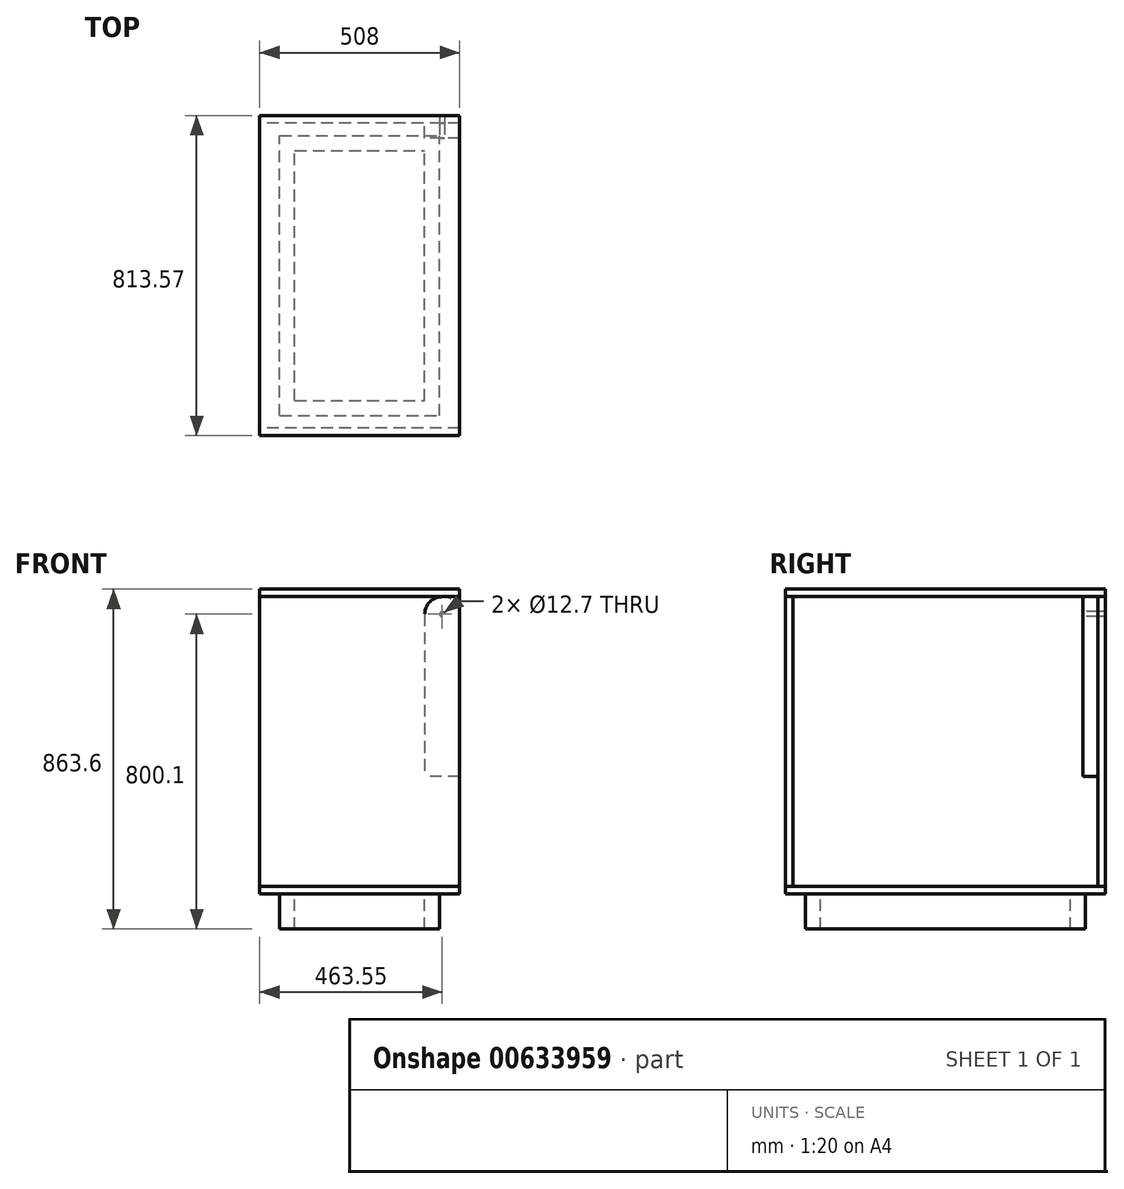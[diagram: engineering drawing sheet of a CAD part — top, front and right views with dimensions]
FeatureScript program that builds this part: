
annotation { "Feature Type Name" : "Feature", "Feature Type Description" : "" }
export const myFeature = defineFeature(function(context is Context, id is Id, definition is map)
    precondition{}
    {
        {
            var Q0;
            Q0=qCreatedBy(makeId("Front.planeOp"),FACE);
            var sketch = newSketch(context, id + "F0", { "sketchPlane" : qUnion([Q0])});
            skLineSegment(sketch, "E0.bottom", {"start": v(0, 0) * mm, "end": v(-508, 0) * mm});
            skLineSegment(sketch, "E0.top", {"start": v(0, -736.6) * mm, "end": v(-508, -736.6) * mm});
            skLineSegment(sketch, "E0.left", {"start": v(0, 0) * mm, "end": v(0, -736.6) * mm});
            skLineSegment(sketch, "E0.right", {"start": v(-508, 0) * mm, "end": v(-508, -736.6) * mm});
            skSolve(sketch);
        }
        {
            var Q0;
            Q0=makeQuery(id+"F0.imprint","IMPRINT",FACE,{"disambiguationData":[TD([[makeQuery(id+"F0.imprint","IMPRINT",EDGE,{"derivedFrom":sQuery(id+"F0.wireOp",EDGE,"E0.bottom")}),1.0]])]});
            extrude(context, id + "F1", {"entities" : qUnion([Q0]), "depth" : 19.05 * mm, "offsetDistance" : 25.4 * mm});
        }
        {
            var Q0;
            Q0=makeQuery(id+"F1.opExtrude","CAP_FACE",FACE,{"disambiguationData":[OSD([sQuery(id+"F0.wireOp",EDGE,"E0.bottom"),sQuery(id+"F0.wireOp",EDGE,"E0.top"),sQuery(id+"F0.wireOp",EDGE,"E0.left"),sQuery(id+"F0.wireOp",EDGE,"E0.right")])],"isStart":true});
            cPlane(context, id + "F2", {"entities" : qUnion([Q0]), "cplaneType" : CPlaneType.OFFSET, "offset" : 793.75 * mm, "width" : 152.4 * mm, "height" : 152.4 * mm});
        }
        {
            var Q0;
            Q0=qCreatedBy(makeId("Top.planeOp"),FACE);
            cPlane(context, id + "F3", {"entities" : qUnion([Q0]), "cplaneType" : CPlaneType.OFFSET, "offset" : 755.65 * mm, "oppositeDirection" : true, "width" : 152.4 * mm, "height" : 152.4 * mm});
        }
        {
            var Q0;
            Q0=qCreatedBy(id+"F2.planeOp",FACE);
            var sketch = newSketch(context, id + "F4", { "sketchPlane" : qUnion([Q0])});
            skLineSegment(sketch, "E1.bottom", {"start": v(0, 0) * mm, "end": v(508, 0) * mm});
            skLineSegment(sketch, "E1.top", {"start": v(0, -736.6) * mm, "end": v(508, -736.6) * mm});
            skLineSegment(sketch, "E1.left", {"start": v(0, 0) * mm, "end": v(0, -736.6) * mm});
            skLineSegment(sketch, "E1.right", {"start": v(508, 0) * mm, "end": v(508, -736.6) * mm});
            skSolve(sketch);
        }
        {
            var Q0;
            Q0=makeQuery(id+"F4.imprint","IMPRINT",FACE,{"disambiguationData":[TD([[makeQuery(id+"F4.imprint","IMPRINT",EDGE,{"derivedFrom":sQuery(id+"F4.wireOp",EDGE,"E1.bottom")}),-1.0]])]});
            extrude(context, id + "F5", {"entities" : qUnion([Q0]), "oppositeDirection" : true, "depth" : 19.05 * mm, "offsetDistance" : 25.4 * mm});
        }
        {
            var Q0;
            Q0=qCreatedBy(makeId("Top.planeOp"),FACE);
            var sketch = newSketch(context, id + "F6", { "sketchPlane" : qUnion([Q0])});
            skLineSegment(sketch, "E2.bottom", {"start": v(0, -18.96) * mm, "end": v(-508, -18.96) * mm});
            skLineSegment(sketch, "E2.top", {"start": v(0, 793.84) * mm, "end": v(-508, 793.84) * mm});
            skLineSegment(sketch, "E2.left", {"start": v(0, -18.96) * mm, "end": v(0, 793.84) * mm});
            skLineSegment(sketch, "E2.right", {"start": v(-508, -18.96) * mm, "end": v(-508, 793.84) * mm});
            skSolve(sketch);
        }
        {
            var Q0;
            Q0=makeQuery(id+"F6.imprint","IMPRINT",FACE,{"disambiguationData":[TD([[makeQuery(id+"F6.imprint","IMPRINT",EDGE,{"derivedFrom":sQuery(id+"F6.wireOp",EDGE,"E2.bottom")}),-1.0]])]});
            extrude(context, id + "F7", {"entities" : qUnion([Q0]), "depth" : 19.05 * mm, "offsetDistance" : 25.4 * mm});
        }
        {
            var Q0;
            Q0=qCreatedBy(id+"F3.planeOp",FACE);
            var sketch = newSketch(context, id + "F8", { "sketchPlane" : qUnion([Q0])});
            skLineSegment(sketch, "E3.bottom", {"start": v(0, -19.73) * mm, "end": v(-508, -19.73) * mm});
            skLineSegment(sketch, "E3.top", {"start": v(0, 793.07) * mm, "end": v(-508, 793.07) * mm});
            skLineSegment(sketch, "E3.left", {"start": v(0, -19.73) * mm, "end": v(0, 793.07) * mm});
            skLineSegment(sketch, "E3.right", {"start": v(-508, -19.73) * mm, "end": v(-508, 793.07) * mm});
            skSolve(sketch);
        }
        {
            var Q0;
            Q0=makeQuery(id+"F8.imprint","IMPRINT",FACE,{"disambiguationData":[TD([[makeQuery(id+"F8.imprint","IMPRINT",EDGE,{"derivedFrom":sQuery(id+"F8.wireOp",EDGE,"E3.bottom")}),-1.0]])]});
            extrude(context, id + "F9", {"entities" : qUnion([Q0]), "depth" : 19.05 * mm, "offsetDistance" : 25.4 * mm});
        }
        {
            var Q0;
            Q0=qCreatedBy(id+"F3.planeOp",FACE);
            var sketch = newSketch(context, id + "F10", { "sketchPlane" : qUnion([Q0])});
            skLineSegment(sketch, "E4.bottom", {"start": v(-457.2, 31.07) * mm, "end": v(-50.8, 31.07) * mm});
            skLineSegment(sketch, "E4.top", {"start": v(-457.2, 742.95) * mm, "end": v(-50.8, 742.95) * mm});
            skLineSegment(sketch, "E4.left", {"start": v(-457.2, 31.07) * mm, "end": v(-457.2, 742.95) * mm});
            skLineSegment(sketch, "E4.right", {"start": v(-50.8, 31.07) * mm, "end": v(-50.8, 742.95) * mm});
            skLineSegment(sketch, "E5.0", {"start": v(-419.1, 69.17) * mm, "end": v(-419.1, 704.85) * mm});
            skLineSegment(sketch, "E5.1", {"start": v(-419.1, 69.17) * mm, "end": v(-88.9, 69.17) * mm});
            skLineSegment(sketch, "E5.2", {"start": v(-88.9, 69.17) * mm, "end": v(-88.9, 704.85) * mm});
            skLineSegment(sketch, "E5.3", {"start": v(-419.1, 704.85) * mm, "end": v(-88.9, 704.85) * mm});
            skSolve(sketch);
        }
        {
            var Q0;
            Q0=makeQuery(id+"F10.imprint","IMPRINT",FACE,{"disambiguationData":[TD([[makeQuery(id+"F10.imprint","IMPRINT",EDGE,{"derivedFrom":sQuery(id+"F10.wireOp",EDGE,"E4.bottom")}),1.0]])]});
            extrude(context, id + "F11", {"entities" : qUnion([Q0]), "operationType" : NewBodyOperationType.ADD, "oppositeDirection" : true, "depth" : 88.9 * mm, "offsetDistance" : 25.4 * mm});
        }
        {
            var Q0;
            Q0=makeQuery(id+"F5.opExtrude","CAP_FACE",FACE,{"disambiguationData":[OSD([sQuery(id+"F4.wireOp",EDGE,"E1.bottom"),sQuery(id+"F4.wireOp",EDGE,"E1.top"),sQuery(id+"F4.wireOp",EDGE,"E1.left"),sQuery(id+"F4.wireOp",EDGE,"E1.right")])],"isStart":false});
            cPlane(context, id + "F12", {"entities" : qUnion([Q0]), "cplaneType" : CPlaneType.OFFSET, "offset" : 0 * mm, "width" : 152.4 * mm, "height" : 152.4 * mm});
        }
        {
            var Q0;
            Q0=qCreatedBy(id+"F12.planeOp",FACE);
            var sketch = newSketch(context, id + "F13", { "sketchPlane" : qUnion([Q0])});
            skLineSegment(sketch, "E6.top", {"start": v(0, -457.2) * mm, "end": v(-88.9, -457.2) * mm});
            skLineSegment(sketch, "E6.left", {"start": v(0, -44.45) * mm, "end": v(0, -457.2) * mm});
            skLineSegment(sketch, "E6.right", {"start": v(-88.9, -44.45) * mm, "end": v(-88.9, -457.2) * mm});
            skArc(sketch, "E7", {"start": v(0, -44.45) * mm, "mid": v(-44.45, 0) * mm, "end": v(-88.9, -44.45) * mm});
            skPoint(sketch, "E7.first.point", {"position": v(-44.45, 0) * mm});
            skPoint(sketch, "E7.second.point", {"position": v(-88.9, -44.45) * mm});
            skPoint(sketch, "E7.third.point", {"position": v(0, -44.45) * mm});
            skPoint(sketch, "E8.orphan", {"position": v(0, 0) * mm});
            skPoint(sketch, "E9.orphan", {"position": v(-88.9, 0) * mm});
            skCircle(sketch, "E10", {"center": v(-412.82, -131.41) * mm, "radius": 94.38 * mm});
            skSolve(sketch);
        }
        {
            var Q0;
            Q0=makeQuery(id+"F13.imprint","IMPRINT",FACE,{"disambiguationData":[TD([[makeQuery(id+"F13.imprint","IMPRINT",EDGE,{"derivedFrom":sQuery(id+"F13.wireOp",EDGE,"E6.top")}),-1.0]])]});
            extrude(context, id + "F14", {"entities" : qUnion([Q0]), "depth" : 38.1 * mm, "offsetDistance" : 25.4 * mm});
        }
        {
            var Q0;
            Q0=makeQuery(id+"F14.opExtrude","CAP_FACE",FACE,{"disambiguationData":[OSD([sQuery(id+"F13.wireOp",EDGE,"E6.top"),sQuery(id+"F13.wireOp",EDGE,"E6.left"),sQuery(id+"F13.wireOp",EDGE,"E6.right"),sQuery(id+"F13.wireOp",EDGE,"E7")])],"isStart":false});
            var sketch = newSketch(context, id + "F15", { "sketchPlane" : qUnion([Q0])});
            skCircle(sketch, "E11", {"center": v(-44.45, -44.45) * mm, "radius": 6.35 * mm});
            skSolve(sketch);
        }
        {
            var Q0;
            Q0=makeQuery(id+"F15.imprint","IMPRINT",FACE,{"disambiguationData":[TD([[makeQuery(id+"F15.imprint","IMPRINT",EDGE,{"derivedFrom":sQuery(id+"F15.wireOp",EDGE,"E11")}),1.0]])]});
            var Q1;
            Q1=makeQuery(id+"F5.opExtrude","SWEPT_BODY",BODY,{"disambiguationData":[OSD([sQuery(id+"F4.wireOp",EDGE,"E1.bottom"),sQuery(id+"F4.wireOp",EDGE,"E1.top"),sQuery(id+"F4.wireOp",EDGE,"E1.left"),sQuery(id+"F4.wireOp",EDGE,"E1.right")])]});
            extrude(context, id + "F16", {"entities" : qUnion([Q0]), "operationType" : NewBodyOperationType.REMOVE, "endBound" : BoundingType.THROUGH_ALL, "oppositeDirection" : true, "depth" : 25.4 * mm, "endBoundEntityBody" : qUnion([Q1]), "offsetDistance" : 25.4 * mm});
        }
    });
